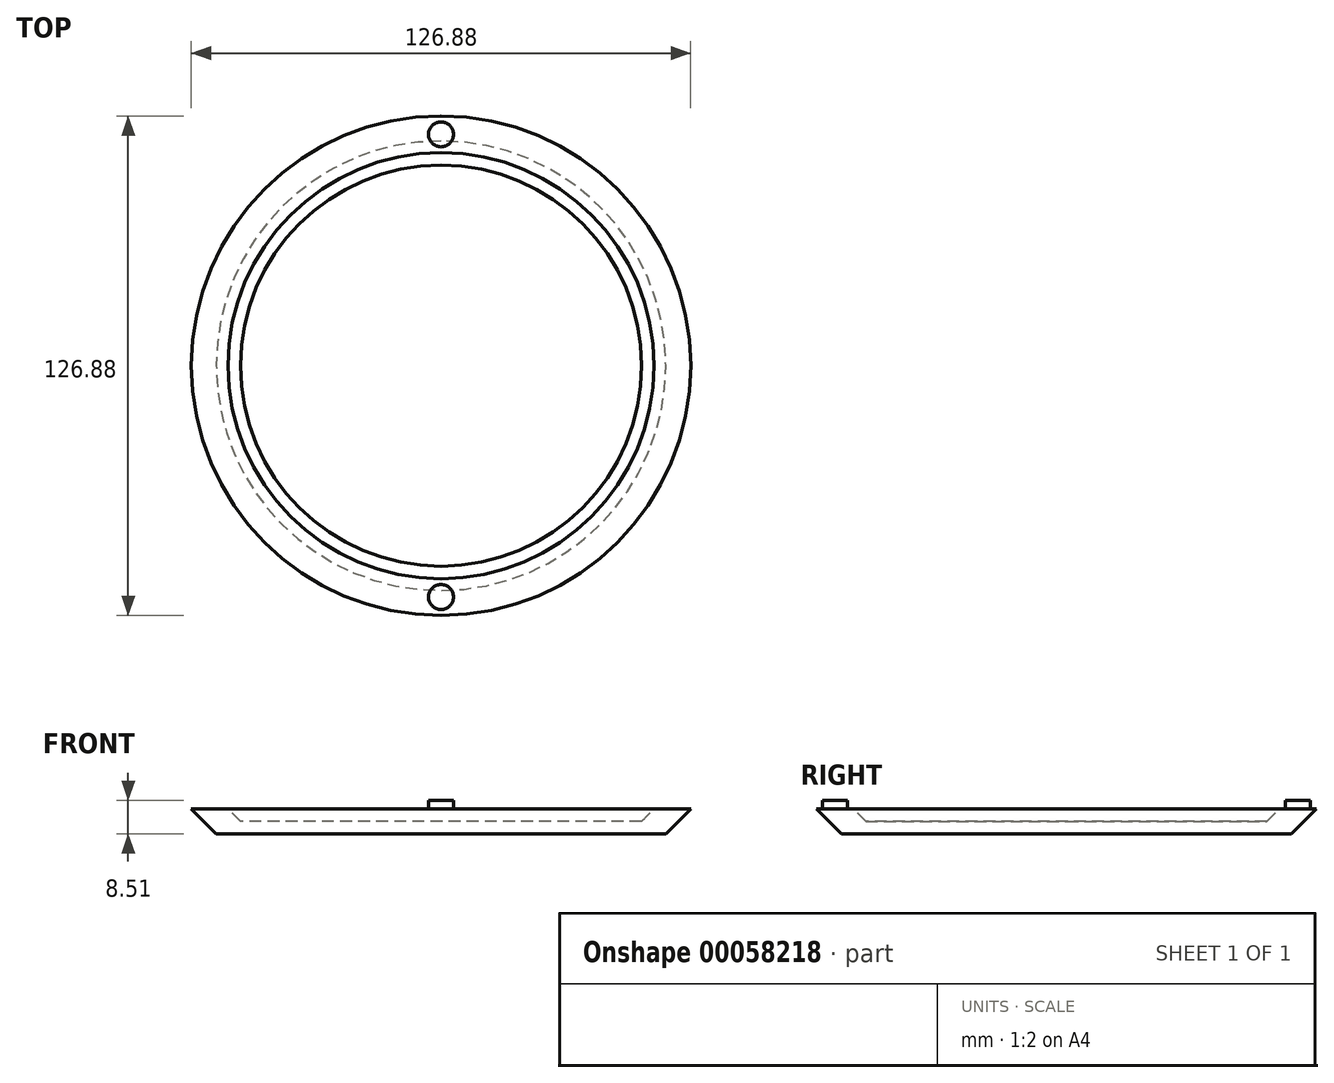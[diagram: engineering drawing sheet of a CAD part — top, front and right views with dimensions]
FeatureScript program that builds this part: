
annotation { "Feature Type Name" : "Feature", "Feature Type Description" : "" }
export const myFeature = defineFeature(function(context is Context, id is Id, definition is map)
    precondition{}
    {
        {
            var Q0;
            Q0=qCreatedBy(makeId("Top.planeOp"),FACE);
            var sketch = newSketch(context, id + "F0", { "sketchPlane" : qUnion([Q0])});
            skCircle(sketch, "E0", {"center": v(0, 0) * mm, "radius": 50.8 * mm});
            skSolve(sketch);
        }
        {
            var Q0;
            Q0=qSketchRegion(id+"F0",true);
            extrude(context, id + "F1", {"entities" : qUnion([Q0]), "oppositeDirection" : true, "depth" : 38.1 * mm, "hasDraft" : true, "draftAngle" : 35 * degree, "draftPullDirection" : true});
        }
        {
            var Q0;
            Q0=makeQuery(id+"F1.opExtrude","CAP_FACE",FACE,{"disambiguationData":[OSD([sQuery(id+"F0.wireOp",EDGE,"E0")])],"isStart":true});
            var sketch = newSketch(context, id + "F2", { "sketchPlane" : qUnion([Q0])});
            skCircle(sketch, "E1", {"center": v(0, 0) * mm, "radius": 44.45 * mm});
            skSolve(sketch);
        }
        {
            var Q0;
            Q0=qSketchRegion(id+"F2",true);
            extrude(context, id + "F3", {"entities" : qUnion([Q0]), "operationType" : NewBodyOperationType.REMOVE, "oppositeDirection" : true, "depth" : 31.75 * mm, "hasDraft" : true, "draftAngle" : 35 * degree, "draftPullDirection" : true});
        }
        {
            var Q0;
            Q0=qCreatedBy(makeId("Right.planeOp"),FACE);
            var sketch = newSketch(context, id + "F4", { "sketchPlane" : qUnion([Q0])});
            skPoint(sketch, "E2", {"position": v(-50.8, 0) * mm});
            skFitSpline(sketch, "E3", {"points": [v(-50.8, 0) * mm, v(-70.84, -31.02) * mm, v(-50.8, -97.59) * mm], "startDerivative": vector(-62.24, -64.04) * mm, "endDerivative": vector(44.05, -127.52) * mm});
            skFitSpline(sketch, "E4.MirrorCS", {"points": [v(50.8, 0) * mm, v(70.84, -31.02) * mm, v(50.8, -97.59) * mm], "startDerivative": vector(62.24, -64.04) * mm, "endDerivative": vector(-44.05, -127.52) * mm});
            skSolve(sketch);
        }
        {
            var Q0;
            Q0=sQuery(id+"F4.wireOp",VERTEX,"E2");
            var Q1;
            Q1=qCreatedBy(makeId("Front.planeOp"),FACE);
            cPlane(context, id + "F5", {"entities" : qUnion([Q0, Q1]), "cplaneType" : CPlaneType.PLANE_POINT, "offset" : 152.4 * mm, "width" : 152.4 * mm, "height" : 152.4 * mm});
        }
        {
            var Q0;
            Q0=qCreatedBy(id+"F5.planeOp",FACE);
            var sketch = newSketch(context, id + "F6", { "sketchPlane" : qUnion([Q0])});
            skCircle(sketch, "E5", {"center": v(0, -6.35) * mm, "radius": 6.35 * mm});
            skSolve(sketch);
        }
        {
            var Q0;
            Q0=makeQuery(id+"F6.imprint","IMPRINT",FACE,{"disambiguationData":[TD([[makeQuery(id+"F6.imprint","IMPRINT",EDGE,{"derivedFrom":sQuery(id+"F6.wireOp",EDGE,"E5")}),1.0]])]});
            var Q1;
            Q1=sQuery(id+"F4.wireOp",EDGE,"E3");
            sweep(context, id + "F7", {"profiles" : qUnion([Q0]), "path" : qUnion([Q1])});
        }
        {
            var Q0;
            Q0=makeQuery(id+"F6.imprint","IMPRINT",FACE,{"disambiguationData":[TD([[makeQuery(id+"F6.imprint","IMPRINT",EDGE,{"derivedFrom":sQuery(id+"F6.wireOp",EDGE,"E5")}),1.0]])]});
            var Q1;
            Q1=makeQuery(id+"F1.opExtrude","SWEPT_FACE",FACE,{"disambiguationData":[OSD([sQuery(id+"F0.wireOp",EDGE,"E0")])]});
            extrude(context, id + "F8", {"entities" : qUnion([Q0]), "endBound" : BoundingType.UP_TO_SURFACE, "oppositeDirection" : true, "endBoundEntityFace" : qUnion([Q1]), "depth" : 25.4 * mm});
        }
        {
            var Q0;
            Q0=makeQuery(id+"F7.opSweep","SWEPT_BODY",BODY,{"disambiguationData":[OSD([sQuery(id+"F4.wireOp",EDGE,"E3"),sQuery(id+"F6.wireOp",EDGE,"E5")])]});
            var Q1;
            Q1=makeQuery(id+"F8.opExtrude","SWEPT_BODY",BODY,{"disambiguationData":[OSD([sQuery(id+"F6.wireOp",EDGE,"E5")])]});
            var Q2;
            Q2=qCreatedBy(makeId("Front.planeOp"),FACE);
            mirror(context, id + "F9", {"operationType" : NewBodyOperationType.ADD, "entities" : qUnion([Q0, Q1]), "mirrorPlane" : qUnion([Q2])});
        }
        {
            var Q0;
            Q0=qCreatedBy(makeId("Right.planeOp"),FACE);
            var sketch = newSketch(context, id + "F10", { "sketchPlane" : qUnion([Q0])});
            skLineSegment(sketch, "E6", {"start": v(0, 0) * mm, "end": v(0, -8.97) * mm});
            skSolve(sketch);
        }
        {
            var Q0;
            Q0=makeQuery(id+"F7.opSweep","CAP_FACE",FACE,{"disambiguationData":[OSD([sQuery(id+"F4.wireOp",VERTEX,"E3.end"),sQuery(id+"F6.wireOp",EDGE,"E5")])],"isStart":false});
            var sketch = newSketch(context, id + "F11", { "sketchPlane" : qUnion([Q0])});
            skPoint(sketch, "E7", {"position": v(0, -11.28) * mm});
            skSolve(sketch);
        }
        {
            var Q0;
            Q0=sQuery(id+"F11.wireOp",VERTEX,"E7");
            var Q1;
            Q1=qCreatedBy(makeId("Top.planeOp"),FACE);
            cPlane(context, id + "F12", {"entities" : qUnion([Q0, Q1]), "cplaneType" : CPlaneType.PLANE_POINT, "offset" : 152.4 * mm, "width" : 152.4 * mm, "height" : 152.4 * mm});
        }
        {
            var Q0;
            Q0=qCreatedBy(id+"F12.planeOp",FACE);
            var sketch = newSketch(context, id + "F13", { "sketchPlane" : qUnion([Q0])});
            skLineSegment(sketch, "E8.bottom", {"start": v(-17.67, -100.3) * mm, "end": v(22.41, -100.3) * mm});
            skLineSegment(sketch, "E8.top", {"start": v(-17.67, 121.35) * mm, "end": v(22.41, 121.35) * mm});
            skLineSegment(sketch, "E8.left", {"start": v(-17.67, -100.3) * mm, "end": v(-17.67, 121.35) * mm});
            skLineSegment(sketch, "E8.right", {"start": v(22.41, -100.3) * mm, "end": v(22.41, 121.35) * mm});
            skSolve(sketch);
        }
        {
            var Q0;
            Q0=qSketchRegion(id+"F13",true);
            extrude(context, id + "F14", {"entities" : qUnion([Q0]), "operationType" : NewBodyOperationType.REMOVE, "depth" : 38.1 * mm});
        }
        {
            var Q0;
            Q0=makeQuery(id+"F14.boolean.opBoolean","COPY",FACE,{"disambiguationData":[TD([makeQuery(id+"F7.opSweep","SWEPT_FACE",FACE,{"disambiguationData":[OSD([sQuery(id+"F4.wireOp",EDGE,"E3"),sQuery(id+"F6.wireOp",EDGE,"E5")])]})])],"derivedFrom":makeQuery(id+"F14.opExtrude","CAP_FACE",FACE,{"disambiguationData":[OSD([sQuery(id+"F13.wireOp",EDGE,"E8.bottom"),sQuery(id+"F13.wireOp",EDGE,"E8.top"),sQuery(id+"F13.wireOp",EDGE,"E8.left"),sQuery(id+"F13.wireOp",EDGE,"E8.right")])],"isStart":false})});
            var sketch = newSketch(context, id + "F15", { "sketchPlane" : qUnion([Q0])});
            skPoint(sketch, "E9", {"position": v(0, 63.44) * mm});
            skSolve(sketch);
        }
        {
            var Q0;
            Q0=makeQuery(id+"F14.boolean.opBoolean","COPY",FACE,{"disambiguationData":[TD([makeQuery(id+"F9.opPattern","COPY",FACE,{"derivedFrom":makeQuery(id+"F7.opSweep","SWEPT_FACE",FACE,{"disambiguationData":[OSD([sQuery(id+"F4.wireOp",EDGE,"E3"),sQuery(id+"F6.wireOp",EDGE,"E5")])]}),"instanceName":"1"})])],"derivedFrom":makeQuery(id+"F14.opExtrude","CAP_FACE",FACE,{"disambiguationData":[OSD([sQuery(id+"F13.wireOp",EDGE,"E8.bottom"),sQuery(id+"F13.wireOp",EDGE,"E8.top"),sQuery(id+"F13.wireOp",EDGE,"E8.left"),sQuery(id+"F13.wireOp",EDGE,"E8.right")])],"isStart":false})});
            var sketch = newSketch(context, id + "F16", { "sketchPlane" : qUnion([Q0])});
            skCircle(sketch, "E10", {"center": v(0, 0) * mm, "radius": 63.44 * mm});
            skSolve(sketch);
        }
        {
            var Q0;
            Q0=qSketchRegion(id+"F16",true);
            extrude(context, id + "F17", {"entities" : qUnion([Q0]), "operationType" : NewBodyOperationType.ADD, "depth" : 6.35 * mm, "hasDraft" : true, "draftAngle" : 45 * degree, "draftPullDirection" : true});
        }
        {
            var Q0;
            Q0=makeQuery(id+"F17.opExtrude","CAP_FACE",FACE,{"disambiguationData":[OSD([sQuery(id+"F16.wireOp",EDGE,"E10")])],"isStart":true});
            var sketch = newSketch(context, id + "F18", { "sketchPlane" : qUnion([Q0])});
            skCircle(sketch, "E11", {"center": v(0, 0) * mm, "radius": 54.12 * mm});
            skSolve(sketch);
        }
        {
            var Q0;
            Q0=qSketchRegion(id+"F18",true);
            extrude(context, id + "F19", {"entities" : qUnion([Q0]), "operationType" : NewBodyOperationType.REMOVE, "oppositeDirection" : true, "depth" : 3.17 * mm, "hasDraft" : true, "draftAngle" : 45 * degree, "draftPullDirection" : true});
        }
        {
            var Q0;
            Q0=makeQuery(id+"F3.boolean.opBoolean","COPY",FACE,{"derivedFrom":makeQuery(id+"F3.opExtrude","CAP_FACE",FACE,{"disambiguationData":[OSD([sQuery(id+"F2.wireOp",EDGE,"E1")])],"isStart":false})});
            var sketch = newSketch(context, id + "F20", { "sketchPlane" : qUnion([Q0])});
            skCircle(sketch, "E12", {"center": v(0, 0) * mm, "radius": 2.38 * mm});
            skSolve(sketch);
        }
        {
            var Q0;
            Q0=qSketchRegion(id+"F20",true);
            extrude(context, id + "F21", {"entities" : qUnion([Q0]), "operationType" : NewBodyOperationType.REMOVE, "endBound" : BoundingType.UP_TO_NEXT, "oppositeDirection" : true, "depth" : 25.4 * mm});
        }
        {
            var Q0;
            Q0=makeQuery(id+"F19.boolean.opBoolean","SPLIT",FACE,{"disambiguationData":[OD(1.0)],"derivedFrom":makeQuery(id+"F17.opExtrude","CAP_FACE",FACE,{"disambiguationData":[OSD([sQuery(id+"F16.wireOp",EDGE,"E10")])],"isStart":true})});
            cPlane(context, id + "F22", {"entities" : qUnion([Q0]), "cplaneType" : CPlaneType.OFFSET, "offset" : 0 * mm, "width" : 152.4 * mm, "height" : 152.4 * mm});
        }
        {
            var Q0;
            Q0=qCreatedBy(id+"F22.planeOp",FACE);
            var sketch = newSketch(context, id + "F23", { "sketchPlane" : qUnion([Q0])});
            skLineSegment(sketch, "E13.rect.bottom", {"start": v(272.39, 141.96) * mm, "end": v(-272.39, 141.96) * mm});
            skLineSegment(sketch, "E13.rect.top", {"start": v(272.39, -141.96) * mm, "end": v(-272.39, -141.96) * mm});
            skLineSegment(sketch, "E13.rect.left", {"start": v(272.39, 141.96) * mm, "end": v(272.39, -141.96) * mm});
            skLineSegment(sketch, "E13.rect.right", {"start": v(-272.39, 141.96) * mm, "end": v(-272.39, -141.96) * mm});
            skPoint(sketch, "E13.rect.middle", {"position": v(0, 0) * mm});
            skSolve(sketch);
        }
        {
            var Q0;
            Q0 = qSketchRegion(id + "F23", true);
            extrude(context, id + "F24", {"entities" : qUnion([Q0]), "operationType" : NewBodyOperationType.REMOVE, "endBound" : BoundingType.THROUGH_ALL, "depth" : 25.4 * mm});
        }
        {
            var Q0;
            {var subQ0=makeQuery(id+"F17.opExtrude","CAP_FACE",FACE,{"disambiguationData":[OSD([sQuery(id+"F16.wireOp",EDGE,"E10")])],"isStart":true});Q0=makeQuery(id+"F24.boolean.opBoolean","MERGE",FACE,{"derivedFrom":[makeQuery(id+"F19.boolean.opBoolean","SPLIT",FACE,{"disambiguationData":[OD(0.0)],"derivedFrom":subQ0}),makeQuery(id+"F19.boolean.opBoolean","SPLIT",FACE,{"disambiguationData":[OD(1.0)],"derivedFrom":subQ0}),makeQuery(id+"F24.opExtrude","CAP_FACE",FACE,{"disambiguationData":[OSD([sQuery(id+"F23.wireOp",EDGE,"E13.rect.bottom"),sQuery(id+"F23.wireOp",EDGE,"E13.rect.top"),sQuery(id+"F23.wireOp",EDGE,"E13.rect.left"),sQuery(id+"F23.wireOp",EDGE,"E13.rect.right")])],"isStart":true})]});}
            var sketch = newSketch(context, id + "F25", { "sketchPlane" : qUnion([Q0])});
            skCircle(sketch, "E14", {"center": v(0, 58.78) * mm, "radius": 3.18 * mm});
            skSolve(sketch);
        }
        {
            var Q0;
            Q0 = qSketchRegion(id + "F25", true);
            extrude(context, id + "F26", {"entities" : qUnion([Q0]), "operationType" : NewBodyOperationType.ADD, "depth" : 2.16 * mm});
        }
        {
            var Q0;
            Q0=makeQuery(id+"F26.opExtrude","SWEPT_FACE",FACE,{"disambiguationData":[OSD([sQuery(id+"F25.wireOp",EDGE,"E14")])]});
            var Q1;
            Q1=makeQuery(id+"F26.opExtrude","CAP_FACE",FACE,{"disambiguationData":[OSD([sQuery(id+"F25.wireOp",EDGE,"E14")])],"isStart":false});
            var Q2;
            Q2=qCreatedBy(makeId("Front.planeOp"),FACE);
            mirror(context, id + "F27", {"faces" : qUnion([Q0, Q1]), "mirrorPlane" : qUnion([Q2]), "patternType" : MirrorType.FACE});
        }
    });
